FCSTD DOCUMENT  (FreeCAD 0.17R11624 (Git))
Label: coil
License: All rights reserved
LicenseURL: http://en.wikipedia.org/wiki/All_rights_reserved
objects: Sketcher::SketchObject×3, Part::Sweep×3, Part::Helix×2, Part::Spiral×1, Part::Compound×1
note: 10 computed .brp shape members not serialized (recipe doc carries the construction recipe); baked Part::Feature solids carry a one-line shape summary decoded from their .brp

FEATURE [Part::Helix] Helix
  Angle = 0
  AttacherType = Attacher::AttachEngine3D
  Height = 39.816
  LocalCoord = 0
  Pitch = 0.711
  Radius = 10.3555
  Style = 1
FEATURE [Part::Spiral] Spiral
  AttacherType = Attacher::AttachEngine3D
  Growth = 0.711
  Placement = pos=(0,0,39.816) rot=(0,0,1;0rad)
  Radius = 10.3555
  Rotations = 1
FEATURE [Part::Helix] Helix001
  Angle = 0
  AttacherType = Attacher::AttachEngine3D
  Height = 39.816
  LocalCoord = 1
  Pitch = 0.711
  Radius = 10.711
  Style = 1
FEATURE [Sketcher::SketchObject] Sketch
  Placement = pos=(0,0,0) rot=(-1,0,0;4.71239rad)
  sketch-geometry (1):
    g0: Circle CenterX=10.3555 CenterY=0 CenterZ=0 NormalX=0 NormalY=0 NormalZ=1 Radius=0.3555
  constraints (3):
    c: Radius(g0) = 0.3555
    c: DistanceY(g-1,g0) = 0
    c: DistanceX(g-1,g0) = 10.3555
FEATURE [Part::Sweep] Sweep
  Frenet = true
  Sections = -> [Sketch]
  Solid = true
  Spine = -> Helix
  Transition = 1
FEATURE [Sketcher::SketchObject] Sketch001
  Placement = pos=(0,0,0) rot=(-1,0,0;4.71239rad)
  sketch-geometry (1):
    g0: Circle CenterX=11.0665 CenterY=0 CenterZ=0 NormalX=0 NormalY=0 NormalZ=1 Radius=0.3555
  constraints (3):
    c: Radius(g0) = 0.3555
    c: DistanceY(g-1,g0) = 0
    c: DistanceX(g-1,g0) = 11.0665
FEATURE [Part::Sweep] Sweep001
  Frenet = true
  Sections = -> [Sketch001]
  Solid = true
  Spine = -> Helix001
  Transition = 1
FEATURE [Sketcher::SketchObject] Sketch002
  Placement = pos=(0,0,0) rot=(-1,0,0;4.71239rad)
  sketch-geometry (1):
    g0: Circle CenterX=10.3555 CenterY=39.816 CenterZ=0 NormalX=0 NormalY=0 NormalZ=1 Radius=0.3555
  constraints (3):
    c: Radius(g0) = 0.3555
    c: DistanceY(g-1,g0) = 39.816
    c: DistanceX(g-1,g0) = 10.3555
FEATURE [Part::Sweep] Sweep002
  Frenet = true
  Sections = -> [Sketch002]
  Solid = true
  Spine = -> Spiral
  Transition = 1
FEATURE [Part::Compound] Compound
  Links = -> [Sweep,Sweep001,Sweep002]
